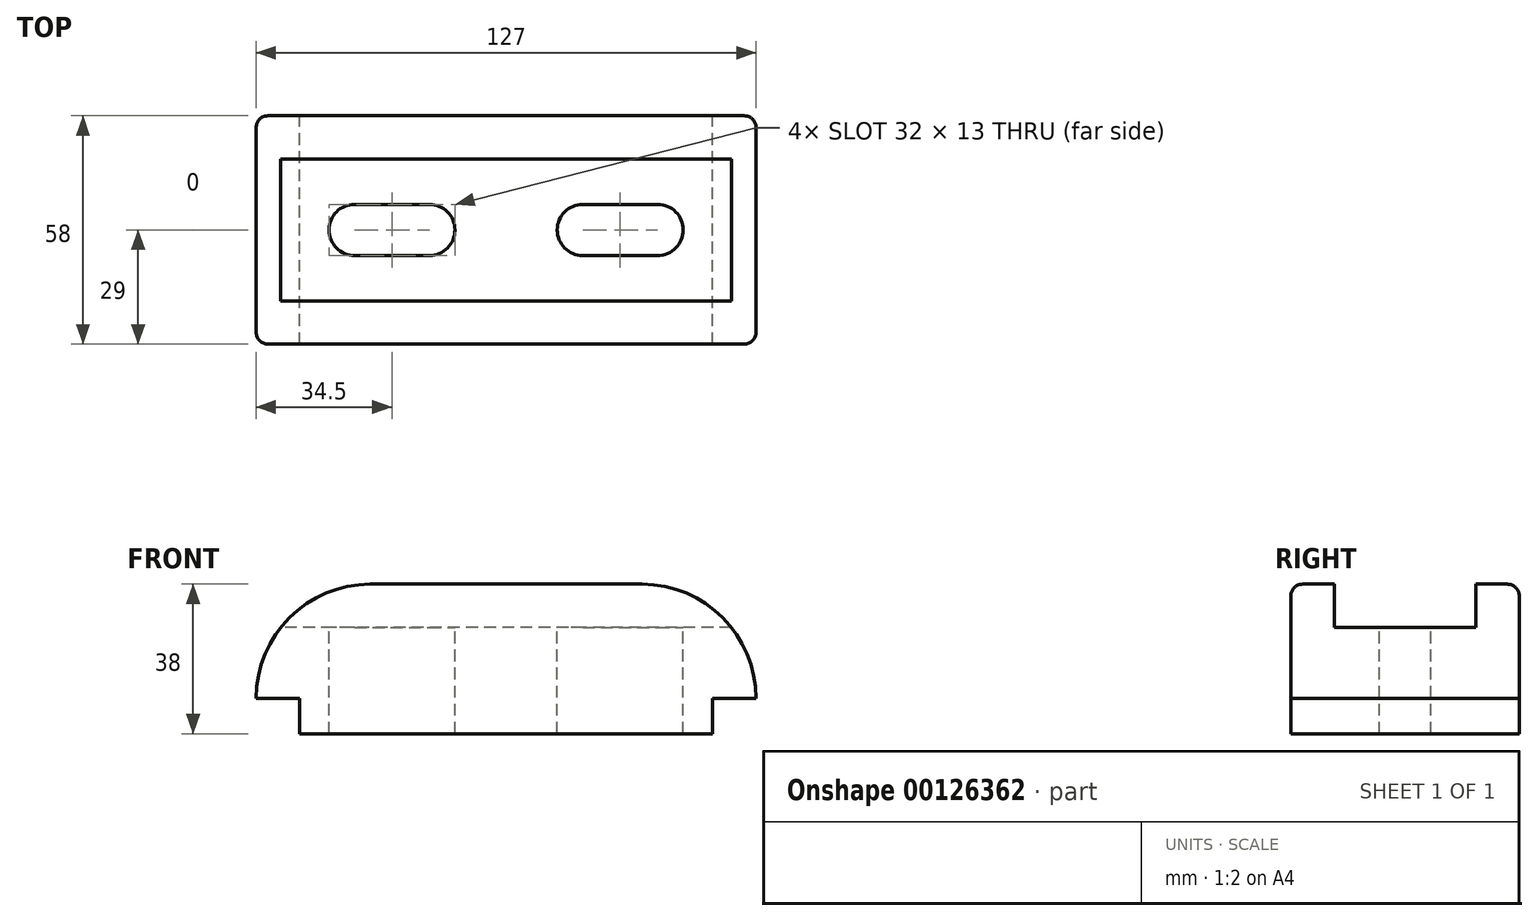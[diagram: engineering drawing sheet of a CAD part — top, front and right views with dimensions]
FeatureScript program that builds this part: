
annotation { "Feature Type Name" : "Feature", "Feature Type Description" : "" }
export const myFeature = defineFeature(function(context is Context, id is Id, definition is map)
    precondition{}
    {
        {
            var Q0;
            Q0=qCreatedBy(makeId("Front.planeOp"),FACE);
            var sketch = newSketch(context, id + "F0", { "sketchPlane" : qUnion([Q0])});
            skLineSegment(sketch, "E0", {"start": v(0, 0) * mm, "end": v(0, 9) * mm});
            skLineSegment(sketch, "E1", {"start": v(0, 9) * mm, "end": v(-11, 9) * mm});
            skLineSegment(sketch, "E2", {"start": v(0, 0) * mm, "end": v(105, 0) * mm});
            skLineSegment(sketch, "E3", {"start": v(105, 0) * mm, "end": v(105, 9) * mm});
            skLineSegment(sketch, "E4", {"start": v(105, 9) * mm, "end": v(116, 9) * mm});
            skLineSegment(sketch, "E5", {"start": v(18, 38) * mm, "end": v(87, 38) * mm});
            skArc(sketch, "E6", {"start": v(18, 38) * mm, "mid": v(-2.5, 29.5) * mm, "end": v(-11, 9) * mm});
            skArc(sketch, "E7", {"start": v(116, 9) * mm, "mid": v(107.5, 29.5) * mm, "end": v(87, 38) * mm});
            skSolve(sketch);
        }
        {
            var Q0;
            Q0 = qSketchRegion(id + "F0", true);
            extrude(context, id + "F1", {"entities" : qUnion([Q0]), "endBound" : BoundingType.SYMMETRIC, "depth" : 58 * mm});
        }
        {
            var Q0;
            Q0=qCreatedBy(makeId("Right.planeOp"),FACE);
            var sketch = newSketch(context, id + "F2", { "sketchPlane" : qUnion([Q0])});
            skLineSegment(sketch, "E8.bottom", {"start": v(-18, 38) * mm, "end": v(18, 38) * mm});
            skLineSegment(sketch, "E8.top", {"start": v(-18, 27) * mm, "end": v(18, 27) * mm});
            skLineSegment(sketch, "E8.left", {"start": v(-18, 38) * mm, "end": v(-18, 27) * mm});
            skLineSegment(sketch, "E8.right", {"start": v(18, 38) * mm, "end": v(18, 27) * mm});
            skSolve(sketch);
        }
        {
            var Q0;
            Q0 = qSketchRegion(id + "F2", true);
            extrude(context, id + "F3", {"entities" : qUnion([Q0]), "operationType" : NewBodyOperationType.REMOVE, "endBound" : BoundingType.THROUGH_ALL, "depth" : 25 * mm});
        }
        {
            var Q0;
            Q0=makeQuery(id+"F3.boolean.opBoolean","COPY",FACE,{"derivedFrom":makeQuery(id+"F3.opExtrude","CAP_FACE",FACE,{"disambiguationData":[OSD([sQuery(id+"F2.wireOp",EDGE,"E8.bottom"),sQuery(id+"F2.wireOp",EDGE,"E8.top"),sQuery(id+"F2.wireOp",EDGE,"E8.left"),sQuery(id+"F2.wireOp",EDGE,"E8.right")])],"isStart":true})});
            extrude(context, id + "F4", {"entities" : qUnion([Q0]), "operationType" : NewBodyOperationType.REMOVE, "endBound" : BoundingType.THROUGH_ALL, "oppositeDirection" : true, "depth" : 25 * mm});
        }
        {
            var Q0;
            {var subQ0=sQuery(id+"F2.wireOp",EDGE,"E8.top");Q0=makeQuery(id+"F4.boolean.opBoolean","MERGE",FACE,{"derivedFrom":[makeQuery(id+"F3.boolean.opBoolean","COPY",FACE,{"derivedFrom":makeQuery(id+"F3.opExtrude","SWEPT_FACE",FACE,{"disambiguationData":[OSD([subQ0])]})}),makeQuery(id+"F4.opExtrude","SWEPT_FACE",FACE,{"disambiguationData":[OSD([subQ0])]})]});}
            var sketch = newSketch(context, id + "F5", { "sketchPlane" : qUnion([Q0])});
            skLineSegment(sketch, "E9", {"start": v(14, 6.5) * mm, "end": v(33, 6.5) * mm});
            skLineSegment(sketch, "E10", {"start": v(14, -6.5) * mm, "end": v(33, -6.5) * mm});
            skLineSegment(sketch, "E11", {"start": v(72, 6.5) * mm, "end": v(91, 6.5) * mm});
            skLineSegment(sketch, "E12", {"start": v(72, -6.5) * mm, "end": v(91, -6.5) * mm});
            skArc(sketch, "E13", {"start": v(33, -6.5) * mm, "mid": v(39.5, 0) * mm, "end": v(33, 6.5) * mm});
            skArc(sketch, "E14", {"start": v(14, 6.5) * mm, "mid": v(7.5, 0) * mm, "end": v(14, -6.5) * mm});
            skArc(sketch, "E15", {"start": v(91, -6.5) * mm, "mid": v(97.5, 0) * mm, "end": v(91, 6.5) * mm});
            skArc(sketch, "E16", {"start": v(72, 6.5) * mm, "mid": v(65.5, 0) * mm, "end": v(72, -6.5) * mm});
            skSolve(sketch);
        }
        {
            var Q0;
            Q0=makeQuery(id+"F5.imprint","IMPRINT",FACE,{"disambiguationData":[TD([[makeQuery(id+"F5.imprint","IMPRINT",EDGE,{"derivedFrom":sQuery(id+"F5.wireOp",EDGE,"E9")}),-1.0]])]});
            var Q1;
            Q1=makeQuery(id+"F5.imprint","IMPRINT",FACE,{"disambiguationData":[TD([[makeQuery(id+"F5.imprint","IMPRINT",EDGE,{"derivedFrom":sQuery(id+"F5.wireOp",EDGE,"E11")}),-1.0]])]});
            extrude(context, id + "F6", {"entities" : qUnion([Q0, Q1]), "operationType" : NewBodyOperationType.REMOVE, "endBound" : BoundingType.THROUGH_ALL, "oppositeDirection" : true, "depth" : 25 * mm});
        }
        {
            var Q0;
            Q0=makeQuery(id+"F1.opExtrude","CAP_EDGE",EDGE,{"disambiguationData":[OSD([sQuery(id+"F0.wireOp",EDGE,"E5")])],"isStart":false});
            var Q1;
            Q1=makeQuery(id+"F1.opExtrude","CAP_EDGE",EDGE,{"disambiguationData":[OSD([sQuery(id+"F0.wireOp",EDGE,"E5")])],"isStart":true});
            fillet(context, id + "F7", {"entities" : qUnion([Q0, Q1]), "radius" : 3 * mm, "tangentPropagation" : true, "allowEdgeOverflow" : false});
        }
    });
